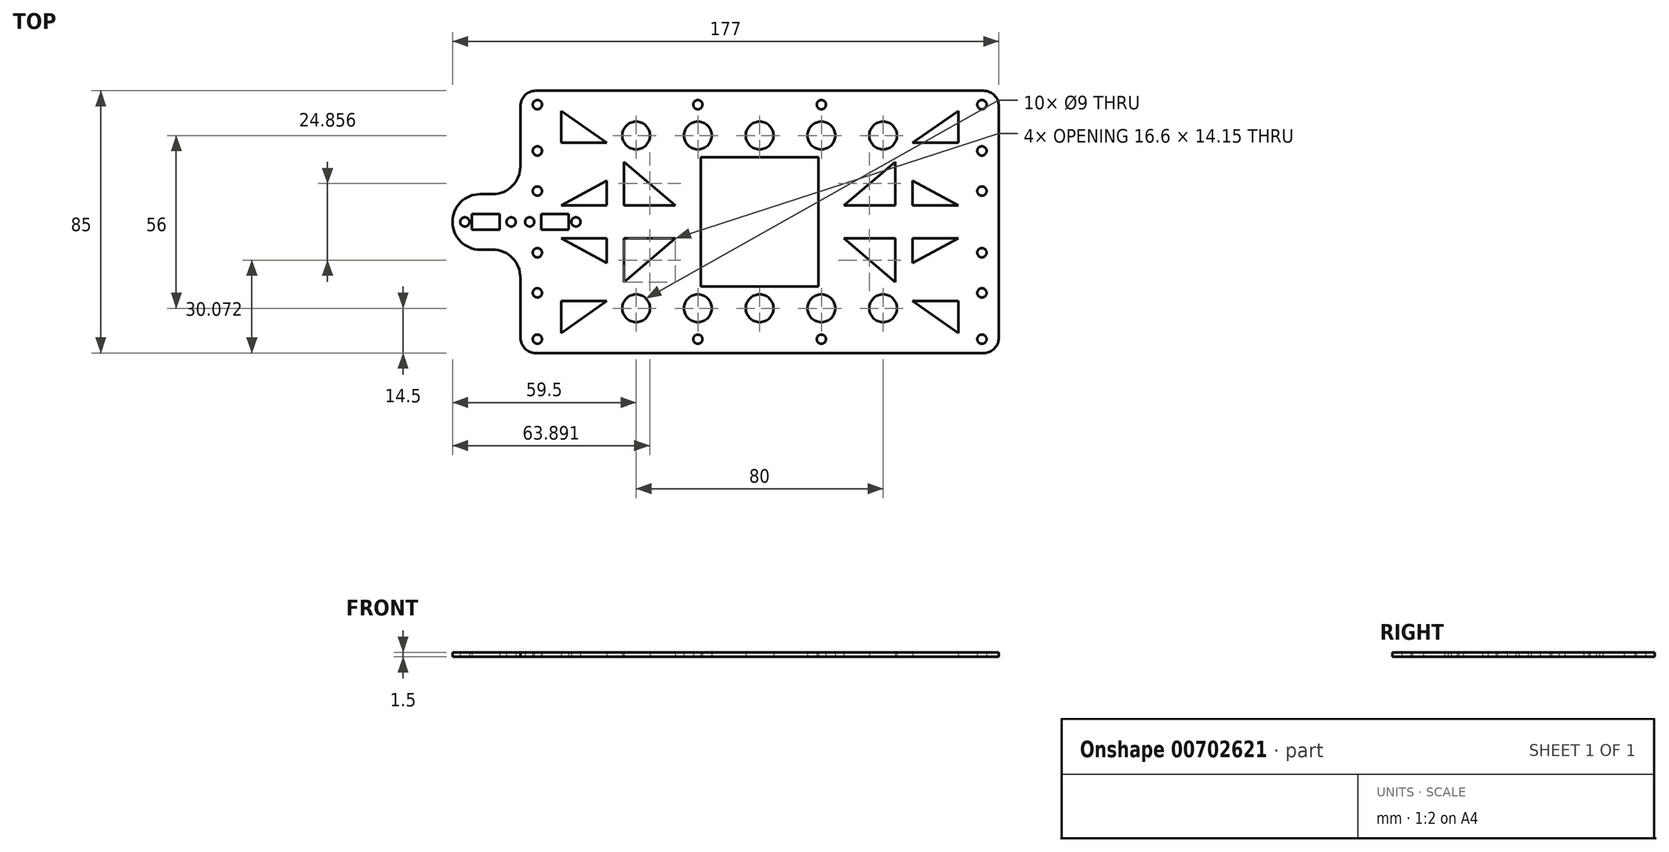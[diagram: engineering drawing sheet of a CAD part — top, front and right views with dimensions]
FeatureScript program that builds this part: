
annotation { "Feature Type Name" : "Feature", "Feature Type Description" : "" }
export const myFeature = defineFeature(function(context is Context, id is Id, definition is map)
    precondition{}
    {
        {
            var Q0;
            Q0=qCreatedBy(makeId("Top.planeOp"),FACE);
            var sketch = newSketch(context, id + "F0", { "sketchPlane" : qUnion([Q0])});
            skLineSegment(sketch, "E0.bottom", {"start": v(77.5, -42.5) * mm, "end": v(-77.5, -42.5) * mm});
            skLineSegment(sketch, "E0.top", {"start": v(77.5, 42.5) * mm, "end": v(-77.5, 42.5) * mm});
            skLineSegment(sketch, "E0.left", {"start": v(77.5, -42.5) * mm, "end": v(77.5, 42.5) * mm});
            skLineSegment(sketch, "E0.right", {"start": v(-77.5, -42.5) * mm, "end": v(-77.5, 42.5) * mm});
            skCircle(sketch, "E1", {"center": v(-72, -10) * mm, "radius": 1.5 * mm});
            skCircle(sketch, "E2", {"center": v(-72, -23) * mm, "radius": 1.5 * mm});
            skCircle(sketch, "E3", {"center": v(-72, -38) * mm, "radius": 1.5 * mm});
            skCircle(sketch, "E4", {"center": v(-20, -38) * mm, "radius": 1.5 * mm});
            skCircle(sketch, "E5", {"center": v(-20, -28) * mm, "radius": 4.5 * mm});
            skCircle(sketch, "E6.MirrorC", {"center": v(20, -28) * mm, "radius": 4.5 * mm});
            skCircle(sketch, "E7.MirrorC", {"center": v(72, -38) * mm, "radius": 1.5 * mm});
            skCircle(sketch, "E8.MirrorC", {"center": v(72, -23) * mm, "radius": 1.5 * mm});
            skCircle(sketch, "E9.MirrorC", {"center": v(72, -10) * mm, "radius": 1.5 * mm});
            skCircle(sketch, "E10.MirrorC", {"center": v(20, -38) * mm, "radius": 1.5 * mm});
            skCircle(sketch, "E11.MirrorC", {"center": v(-72, 10) * mm, "radius": 1.5 * mm});
            skCircle(sketch, "E12.MirrorC", {"center": v(-72, 23) * mm, "radius": 1.5 * mm});
            skCircle(sketch, "E13.MirrorC", {"center": v(-72, 38) * mm, "radius": 1.5 * mm});
            skCircle(sketch, "E14.MirrorC", {"center": v(-20, 28) * mm, "radius": 4.5 * mm});
            skCircle(sketch, "E15.MirrorC", {"center": v(-20, 38) * mm, "radius": 1.5 * mm});
            skCircle(sketch, "E16.MirrorC", {"center": v(20, 28) * mm, "radius": 4.5 * mm});
            skCircle(sketch, "E17.MirrorC", {"center": v(20, 38) * mm, "radius": 1.5 * mm});
            skCircle(sketch, "E18.MirrorC", {"center": v(72, 38) * mm, "radius": 1.5 * mm});
            skCircle(sketch, "E19.MirrorC", {"center": v(72, 23) * mm, "radius": 1.5 * mm});
            skCircle(sketch, "E20.MirrorC", {"center": v(72, 10) * mm, "radius": 1.5 * mm});
            skCircle(sketch, "E21", {"center": v(0, -28) * mm, "radius": 4.5 * mm});
            skLineSegment(sketch, "E22", {"start": v(20, 28) * mm, "end": v(20, -28) * mm, "construction": true});
            skCircle(sketch, "E23.MirrorC", {"center": v(0, 28) * mm, "radius": 4.5 * mm});
            skCircle(sketch, "E24.MirrorC", {"center": v(40, 28) * mm, "radius": 4.5 * mm});
            skCircle(sketch, "E25.MirrorC", {"center": v(40, -28) * mm, "radius": 4.5 * mm});
            skCircle(sketch, "E26.MirrorC", {"center": v(-40, 28) * mm, "radius": 4.5 * mm});
            skCircle(sketch, "E27.MirrorC", {"center": v(-40, -28) * mm, "radius": 4.5 * mm});
            skLineSegment(sketch, "E28", {"start": v(-64.32, -36.02) * mm, "end": v(-49.48, -25.63) * mm});
            skLineSegment(sketch, "E29", {"start": v(-49.48, -25.63) * mm, "end": v(-64.32, -25.63) * mm});
            skLineSegment(sketch, "E30", {"start": v(-64.32, -25.63) * mm, "end": v(-64.32, -36.02) * mm});
            skLineSegment(sketch, "E31", {"start": v(-64.32, -5.35) * mm, "end": v(-49.48, -5.35) * mm});
            skLineSegment(sketch, "E32", {"start": v(-49.48, -5.35) * mm, "end": v(-49.48, -13.35) * mm});
            skLineSegment(sketch, "E33", {"start": v(-49.48, -13.35) * mm, "end": v(-64.32, -5.35) * mm});
            skLineSegment(sketch, "E34", {"start": v(-40, -28) * mm, "end": v(40, -28) * mm, "construction": true});
            skLineSegment(sketch, "E35.MirrorCS", {"start": v(49.48, -13.35) * mm, "end": v(64.32, -5.35) * mm});
            skLineSegment(sketch, "E36.MirrorCS", {"start": v(64.32, -5.35) * mm, "end": v(49.48, -5.35) * mm});
            skLineSegment(sketch, "E37.MirrorCS", {"start": v(49.48, -5.35) * mm, "end": v(49.48, -13.35) * mm});
            skLineSegment(sketch, "E38.MirrorCS", {"start": v(49.48, -25.63) * mm, "end": v(64.32, -25.63) * mm});
            skLineSegment(sketch, "E39.MirrorCS", {"start": v(64.32, -36.02) * mm, "end": v(49.48, -25.63) * mm});
            skLineSegment(sketch, "E40.MirrorCS", {"start": v(64.32, -25.63) * mm, "end": v(64.32, -36.02) * mm});
            skLineSegment(sketch, "E41.MirrorCS", {"start": v(-64.32, 5.35) * mm, "end": v(-49.48, 5.35) * mm});
            skLineSegment(sketch, "E42.MirrorCS", {"start": v(-49.48, 13.35) * mm, "end": v(-64.32, 5.35) * mm});
            skLineSegment(sketch, "E43.MirrorCS", {"start": v(-49.48, 5.35) * mm, "end": v(-49.48, 13.35) * mm});
            skLineSegment(sketch, "E44.MirrorCS", {"start": v(-49.48, 25.63) * mm, "end": v(-64.32, 25.63) * mm});
            skLineSegment(sketch, "E45.MirrorCS", {"start": v(-64.32, 25.63) * mm, "end": v(-64.32, 36.02) * mm});
            skLineSegment(sketch, "E46.MirrorCS", {"start": v(-64.32, 36.02) * mm, "end": v(-49.48, 25.63) * mm});
            skLineSegment(sketch, "E47.MirrorCS", {"start": v(49.48, 13.35) * mm, "end": v(64.32, 5.35) * mm});
            skLineSegment(sketch, "E48.MirrorCS", {"start": v(64.32, 5.35) * mm, "end": v(49.48, 5.35) * mm});
            skLineSegment(sketch, "E49.MirrorCS", {"start": v(49.48, 5.35) * mm, "end": v(49.48, 13.35) * mm});
            skLineSegment(sketch, "E50.MirrorCS", {"start": v(49.48, 25.63) * mm, "end": v(64.32, 25.63) * mm});
            skLineSegment(sketch, "E51.MirrorCS", {"start": v(64.32, 36.02) * mm, "end": v(49.48, 25.63) * mm});
            skLineSegment(sketch, "E52.MirrorCS", {"start": v(64.32, 25.63) * mm, "end": v(64.32, 36.02) * mm});
            skCircle(sketch, "E53", {"center": v(-74.5, 0) * mm, "radius": 1.5 * mm});
            skPoint(sketch, "E53.centerSnap0", {"position": v(-77.5, 0) * mm});
            skCircle(sketch, "E54", {"center": v(-59.5, 0) * mm, "radius": 1.5 * mm});
            skLineSegment(sketch, "E55.bottom", {"start": v(-70.8, 2.5) * mm, "end": v(-61.8, 2.5) * mm});
            skLineSegment(sketch, "E55.top", {"start": v(-70.8, -2.5) * mm, "end": v(-61.8, -2.5) * mm});
            skLineSegment(sketch, "E55.left", {"start": v(-70.8, 2.5) * mm, "end": v(-70.8, -2.5) * mm});
            skLineSegment(sketch, "E55.right", {"start": v(-61.8, 2.5) * mm, "end": v(-61.8, -2.5) * mm});
            skLineSegment(sketch, "E56.bottom", {"start": v(-77.5, -9) * mm, "end": v(-99.5, -9) * mm});
            skLineSegment(sketch, "E56.top", {"start": v(-77.5, 9) * mm, "end": v(-99.5, 9) * mm});
            skLineSegment(sketch, "E56.left", {"start": v(-77.5, -9) * mm, "end": v(-77.5, 9) * mm});
            skLineSegment(sketch, "E56.right", {"start": v(-99.5, -9) * mm, "end": v(-99.5, 9) * mm});
            skCircle(sketch, "E57.MirrorC", {"center": v(-80.5, 0) * mm, "radius": 1.5 * mm});
            skLineSegment(sketch, "E58.MirrorCS", {"start": v(-84.2, 2.5) * mm, "end": v(-84.2, -2.5) * mm});
            skLineSegment(sketch, "E59.MirrorCS", {"start": v(-84.2, 2.5) * mm, "end": v(-93.2, 2.5) * mm});
            skLineSegment(sketch, "E60.MirrorCS", {"start": v(-84.2, -2.5) * mm, "end": v(-93.2, -2.5) * mm});
            skLineSegment(sketch, "E61.MirrorCS", {"start": v(-93.2, 2.5) * mm, "end": v(-93.2, -2.5) * mm});
            skCircle(sketch, "E62.MirrorC", {"center": v(-95.5, 0) * mm, "radius": 1.5 * mm});
            skLineSegment(sketch, "E63.bottom", {"start": v(19, -21) * mm, "end": v(-19, -21) * mm});
            skLineSegment(sketch, "E63.top", {"start": v(19, 21) * mm, "end": v(-19, 21) * mm});
            skLineSegment(sketch, "E63.left", {"start": v(19, -21) * mm, "end": v(19, 21) * mm});
            skLineSegment(sketch, "E63.right", {"start": v(-19, -21) * mm, "end": v(-19, 21) * mm});
            skPoint(sketch, "E63.middle", {"position": v(0, 0) * mm});
            skLineSegment(sketch, "E64", {"start": v(-43.91, 19.5) * mm, "end": v(-43.91, 5.35) * mm});
            skLineSegment(sketch, "E65", {"start": v(-43.91, 5.35) * mm, "end": v(-27.3, 5.35) * mm});
            skLineSegment(sketch, "E66", {"start": v(-27.3, 5.35) * mm, "end": v(-43.91, 19.5) * mm});
            skLineSegment(sketch, "E67.MirrorCS", {"start": v(-43.91, -5.35) * mm, "end": v(-27.3, -5.35) * mm});
            skLineSegment(sketch, "E68.MirrorCS", {"start": v(-43.91, -19.5) * mm, "end": v(-43.91, -5.35) * mm});
            skLineSegment(sketch, "E69.MirrorCS", {"start": v(-27.3, -5.35) * mm, "end": v(-43.91, -19.5) * mm});
            skLineSegment(sketch, "E70.MirrorCS", {"start": v(43.91, 5.35) * mm, "end": v(27.3, 5.35) * mm});
            skLineSegment(sketch, "E71.MirrorCS", {"start": v(43.91, 19.5) * mm, "end": v(43.91, 5.35) * mm});
            skLineSegment(sketch, "E72.MirrorCS", {"start": v(27.3, 5.35) * mm, "end": v(43.91, 19.5) * mm});
            skLineSegment(sketch, "E73.MirrorCS", {"start": v(27.3, -5.35) * mm, "end": v(43.91, -19.5) * mm});
            skLineSegment(sketch, "E74.MirrorCS", {"start": v(43.91, -19.5) * mm, "end": v(43.91, -5.35) * mm});
            skLineSegment(sketch, "E75.MirrorCS", {"start": v(43.91, -5.35) * mm, "end": v(27.3, -5.35) * mm});
            skSolve(sketch);
        }
        {
            var Q0;
            Q0=makeQuery(id+"F0.imprint","IMPRINT",FACE,{"disambiguationData":[TD([[makeQuery(id+"F0.imprint","IMPRINT",EDGE,{"derivedFrom":sQuery(id+"F0.wireOp",EDGE,"E0.bottom")}),-1.0]])]});
            var Q1;
            Q1=makeQuery(id+"F0.imprint","IMPRINT",FACE,{"disambiguationData":[TD([[makeQuery(id+"F0.imprint","IMPRINT",EDGE,{"derivedFrom":sQuery(id+"F0.wireOp",EDGE,"E56.bottom")}),-1.0]])]});
            extrude(context, id + "F1", {"entities" : qUnion([Q0, Q1]), "depth" : 1.5 * mm, "offsetDistance" : 25 * mm});
        }
        {
            var Q0;
            Q0=makeQuery(id+"F1.opExtrude","SWEPT_EDGE",EDGE,{"disambiguationData":[OSD([sQuery(id+"F0.wireOp",EDGE,"E0.top"),sQuery(id+"F0.wireOp",EDGE,"E0.right")])]});
            var Q1;
            Q1=makeQuery(id+"F1.opExtrude","SWEPT_EDGE",EDGE,{"disambiguationData":[OSD([sQuery(id+"F0.wireOp",EDGE,"E0.top"),sQuery(id+"F0.wireOp",EDGE,"E0.left")])]});
            var Q2;
            Q2=makeQuery(id+"F1.opExtrude","SWEPT_EDGE",EDGE,{"disambiguationData":[OSD([sQuery(id+"F0.wireOp",EDGE,"E0.bottom"),sQuery(id+"F0.wireOp",EDGE,"E0.left")])]});
            var Q3;
            Q3=makeQuery(id+"F1.opExtrude","SWEPT_EDGE",EDGE,{"disambiguationData":[OSD([sQuery(id+"F0.wireOp",EDGE,"E0.bottom"),sQuery(id+"F0.wireOp",EDGE,"E0.right")])]});
            fillet(context, id + "F2", {"entities" : qUnion([Q0, Q1, Q2, Q3]), "radius" : 5 * mm, "tangentPropagation" : true, "allowEdgeOverflow" : false});
        }
        {
            var Q0;
            Q0=makeQuery(id+"F1.opExtrude","SWEPT_EDGE",EDGE,{"disambiguationData":[OSD([sQuery(id+"F0.wireOp",EDGE,"E0.right"),sQuery(id+"F0.wireOp",EDGE,"E56.bottom"),sQuery(id+"F0.wireOp",EDGE,"E56.left")])]});
            var Q1;
            Q1=makeQuery(id+"F1.opExtrude","SWEPT_EDGE",EDGE,{"disambiguationData":[OSD([sQuery(id+"F0.wireOp",EDGE,"E0.right"),sQuery(id+"F0.wireOp",EDGE,"E56.top"),sQuery(id+"F0.wireOp",EDGE,"E56.left")])]});
            var Q2;
            Q2=makeQuery(id+"F1.opExtrude","SWEPT_EDGE",EDGE,{"disambiguationData":[OSD([sQuery(id+"F0.wireOp",EDGE,"E56.bottom"),sQuery(id+"F0.wireOp",EDGE,"E56.right")])]});
            var Q3;
            Q3=makeQuery(id+"F1.opExtrude","SWEPT_EDGE",EDGE,{"disambiguationData":[OSD([sQuery(id+"F0.wireOp",EDGE,"E56.top"),sQuery(id+"F0.wireOp",EDGE,"E56.right")])]});
            fillet(context, id + "F3", {"entities" : qUnion([Q0, Q1, Q2, Q3]), "radius" : 9 * mm, "tangentPropagation" : true, "allowEdgeOverflow" : false});
        }
    });
